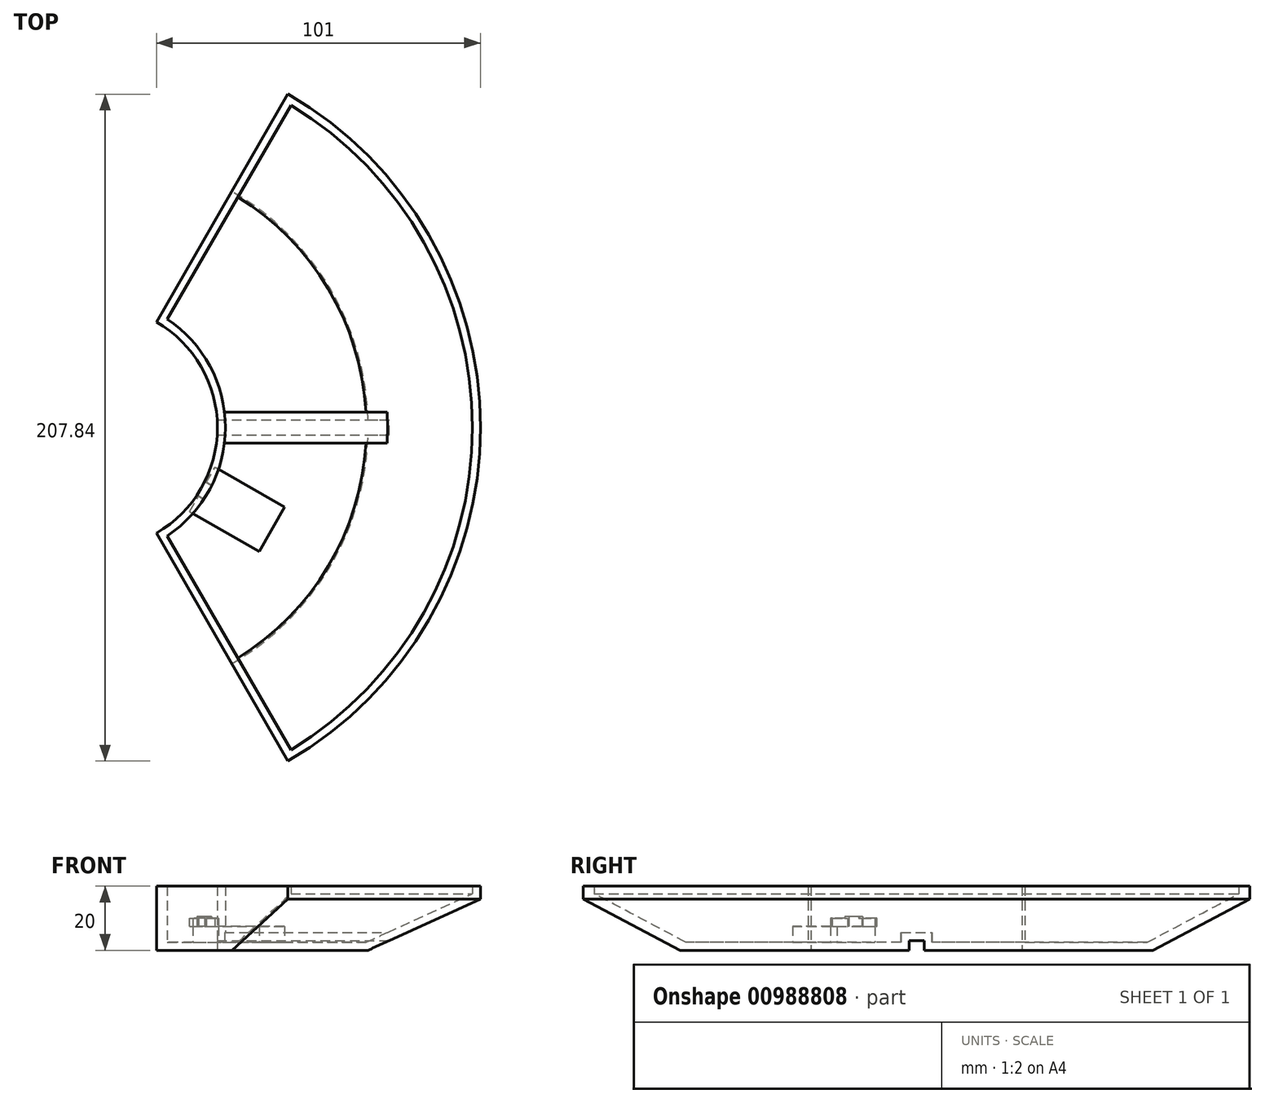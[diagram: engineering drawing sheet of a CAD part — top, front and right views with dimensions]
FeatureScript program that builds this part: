
annotation { "Feature Type Name" : "Feature", "Feature Type Description" : "" }
export const myFeature = defineFeature(function(context is Context, id is Id, definition is map)
    precondition{}
    {
        {
            var Q0;
            Q0=qCreatedBy(makeId("Front.planeOp"),FACE);
            var sketch = newSketch(context, id + "F0", { "sketchPlane" : qUnion([Q0])});
            skLineSegment(sketch, "E0", {"start": v(0, 0) * mm, "end": v(38, 0) * mm, "construction": true});
            skLineSegment(sketch, "E1", {"start": v(38, 0) * mm, "end": v(85, 0) * mm});
            skLineSegment(sketch, "E2", {"start": v(85, 0) * mm, "end": v(120, 16) * mm});
            skLineSegment(sketch, "E3", {"start": v(120, 16) * mm, "end": v(120, 20) * mm});
            skLineSegment(sketch, "E4", {"start": v(120, 20) * mm, "end": v(38, 20) * mm});
            skLineSegment(sketch, "E5", {"start": v(38, 20) * mm, "end": v(38, 0) * mm});
            skSolve(sketch);
        }
        {
            var Q0;
            Q0=qCreatedBy(makeId("Front.planeOp"),FACE);
            var sketch = newSketch(context, id + "F1", { "sketchPlane" : qUnion([Q0])});
            skLineSegment(sketch, "E6", {"start": v(0, 0) * mm, "end": v(0, 70.13) * mm, "construction": true});
            skSolve(sketch);
        }
        {
            var Q0;
            Q0 = qSketchRegion(id + "F0", true);
            var Q1;
            Q1=sQuery(id+"F1.wireOp",EDGE,"E6");
            revolve(context, id + "F2", {"surfaceOperationType" : NewSurfaceOperationType.NEW, "entities" : qUnion([Q0]), "axis" : qUnion([Q1]), "revolveType" : RevolveType.SYMMETRIC, "angle" : 120 * degree});
        }
        {
            var Q0;
            Q0=qCreatedBy(makeId("Top.planeOp"),FACE);
            var sketch = newSketch(context, id + "F3", { "sketchPlane" : qUnion([Q0])});
            skLineSegment(sketch, "E7.bottom", {"start": v(0, 2.35) * mm, "end": v(160, 2.35) * mm});
            skLineSegment(sketch, "E7.top", {"start": v(0, -2.35) * mm, "end": v(160, -2.35) * mm});
            skLineSegment(sketch, "E7.left", {"start": v(0, 2.35) * mm, "end": v(0, -2.35) * mm});
            skLineSegment(sketch, "E7.right", {"start": v(160, 2.35) * mm, "end": v(160, -2.35) * mm});
            skSolve(sketch);
        }
        {
            var Q0;
            Q0 = qSketchRegion(id + "F3", true);
            extrude(context, id + "F4", {"entities" : qUnion([Q0]), "operationType" : NewBodyOperationType.REMOVE, "depth" : 3 * mm, "offsetDistance" : 25 * mm});
        }
        {
            var Q0;
            Q0=makeQuery(id+"F2.opRevolve","SWEPT_FACE",FACE,{"disambiguationData":[OSD([sQuery(id+"F0.wireOp",EDGE,"E4")])]});
            shell(context, id + "F5", {"entities" : qUnion([Q0]), "thickness" : 2.5 * mm});
        }
        {
            var Q0;
            {var subQ2=sQuery(id+"F0.wireOp",EDGE,"E1");Q0=makeQuery(id+"F5.opShell","OFFSET_FACE",FACE,{"disambiguationData":[OSD([subQ2]),TDD([makeQuery(id+"F4.boolean.opBoolean","SPLIT",FACE,{"disambiguationData":[TD([makeQuery(id+"F4.opExtrude","SWEPT_FACE",FACE,{"disambiguationData":[OSD([sQuery(id+"F3.wireOp",EDGE,"E7.top")])]})])],"derivedFrom":makeQuery(id+"F2.opRevolve","SWEPT_FACE",FACE,{"disambiguationData":[OSD([subQ2])]})})])]});}
            var sketch = newSketch(context, id + "F6", { "sketchPlane" : qUnion([Q0])});
            skArc(sketch, "E8.0.0", {"start": v(40.2, -4.85) * mm, "mid": v(34.47, -21.26) * mm, "end": v(22.38, -33.76) * mm});
            skLineSegment(sketch, "E8.0.1", {"start": v(22.38, -33.76) * mm, "end": v(44.37, -71.86) * mm});
            skArc(sketch, "E8.0.2", {"start": v(44.37, -71.86) * mm, "mid": v(72.55, -43.24) * mm, "end": v(84.32, -4.85) * mm});
            skLineSegment(sketch, "E8.0.3", {"start": v(84.32, -4.85) * mm, "end": v(40.2, -4.85) * mm});
            skLineSegment(sketch, "E9", {"start": v(0, 0) * mm, "end": v(73.14, -42.23) * mm, "construction": true});
            skLineSegment(sketch, "E10", {"start": v(37.34, -12.32) * mm, "end": v(29.34, -26.18) * mm});
            skLineSegment(sketch, "E11", {"start": v(29.34, -26.18) * mm, "end": v(51, -38.68) * mm});
            skLineSegment(sketch, "E12", {"start": v(51, -38.68) * mm, "end": v(59, -24.82) * mm});
            skLineSegment(sketch, "E13", {"start": v(59, -24.82) * mm, "end": v(37.34, -12.32) * mm});
            skSolve(sketch);
        }
        {
            var Q0;
            {var subQ0=sQuery(id+"F6.wireOp",EDGE,"E11");Q0=makeQuery(id+"F6.imprint","IMPRINT",FACE,{"disambiguationData":[TD([[makeQuery(id+"F6.imprint","IMPRINT",EDGE,{"derivedFrom":subQ0}),1.0]])]});}
            extrude(context, id + "F7", {"entities" : qUnion([Q0]), "operationType" : NewBodyOperationType.ADD, "depth" : 5 * mm, "offsetDistance" : 25 * mm});
        }
        {
            var Q0;
            Q0=makeQuery(id+"F7.opExtrude","SWEPT_FACE",FACE,{"disambiguationData":[OSD([sQuery(id+"F6.wireOp",EDGE,"E12")])]});
            var sketch = newSketch(context, id + "F8", { "sketchPlane" : qUnion([Q0])});
            skLineSegment(sketch, "E14.bottom", {"start": v(-2.5, 7.5) * mm, "end": v(2.5, 7.5) * mm});
            skLineSegment(sketch, "E14.top", {"start": v(-2.5, 10.5) * mm, "end": v(2.5, 10.5) * mm});
            skLineSegment(sketch, "E14.left", {"start": v(-2.5, 7.5) * mm, "end": v(-2.5, 10.5) * mm});
            skLineSegment(sketch, "E14.right", {"start": v(2.5, 7.5) * mm, "end": v(2.5, 10.5) * mm});
            skSolve(sketch);
        }
        {
            var Q0;
            Q0 = qSketchRegion(id + "F8", true);
            extrude(context, id + "F9", {"entities" : qUnion([Q0]), "operationType" : NewBodyOperationType.REMOVE, "endBound" : BoundingType.THROUGH_ALL, "oppositeDirection" : true, "depth" : 25 * mm, "offsetDistance" : 25 * mm});
        }
        {
            var Q0;
            Q0=makeQuery(id+"F7.opExtrude","SWEPT_FACE",FACE,{"disambiguationData":[OSD([sQuery(id+"F6.wireOp",EDGE,"E12")])]});
            var sketch = newSketch(context, id + "F10", { "sketchPlane" : qUnion([Q0])});
            skLineSegment(sketch, "E15.bottom", {"start": v(-8, 7.5) * mm, "end": v(8, 7.5) * mm});
            skLineSegment(sketch, "E15.top", {"start": v(-8, 10) * mm, "end": v(8, 10) * mm});
            skLineSegment(sketch, "E15.left", {"start": v(-8, 7.5) * mm, "end": v(-8, 10) * mm});
            skLineSegment(sketch, "E15.right", {"start": v(8, 7.5) * mm, "end": v(8, 10) * mm});
            skSolve(sketch);
        }
        {
            var Q0;
            Q0=makeQuery(id+"F10.imprint","IMPRINT",FACE,{"disambiguationData":[TD([[makeQuery(id+"F10.imprint","IMPRINT",EDGE,{"derivedFrom":sQuery(id+"F10.wireOp",EDGE,"E15.bottom")}),1.0]])]});
            extrude(context, id + "F11", {"entities" : qUnion([Q0]), "operationType" : NewBodyOperationType.REMOVE, "oppositeDirection" : true, "depth" : 25 * mm, "offsetDistance" : 25 * mm});
        }
    });
